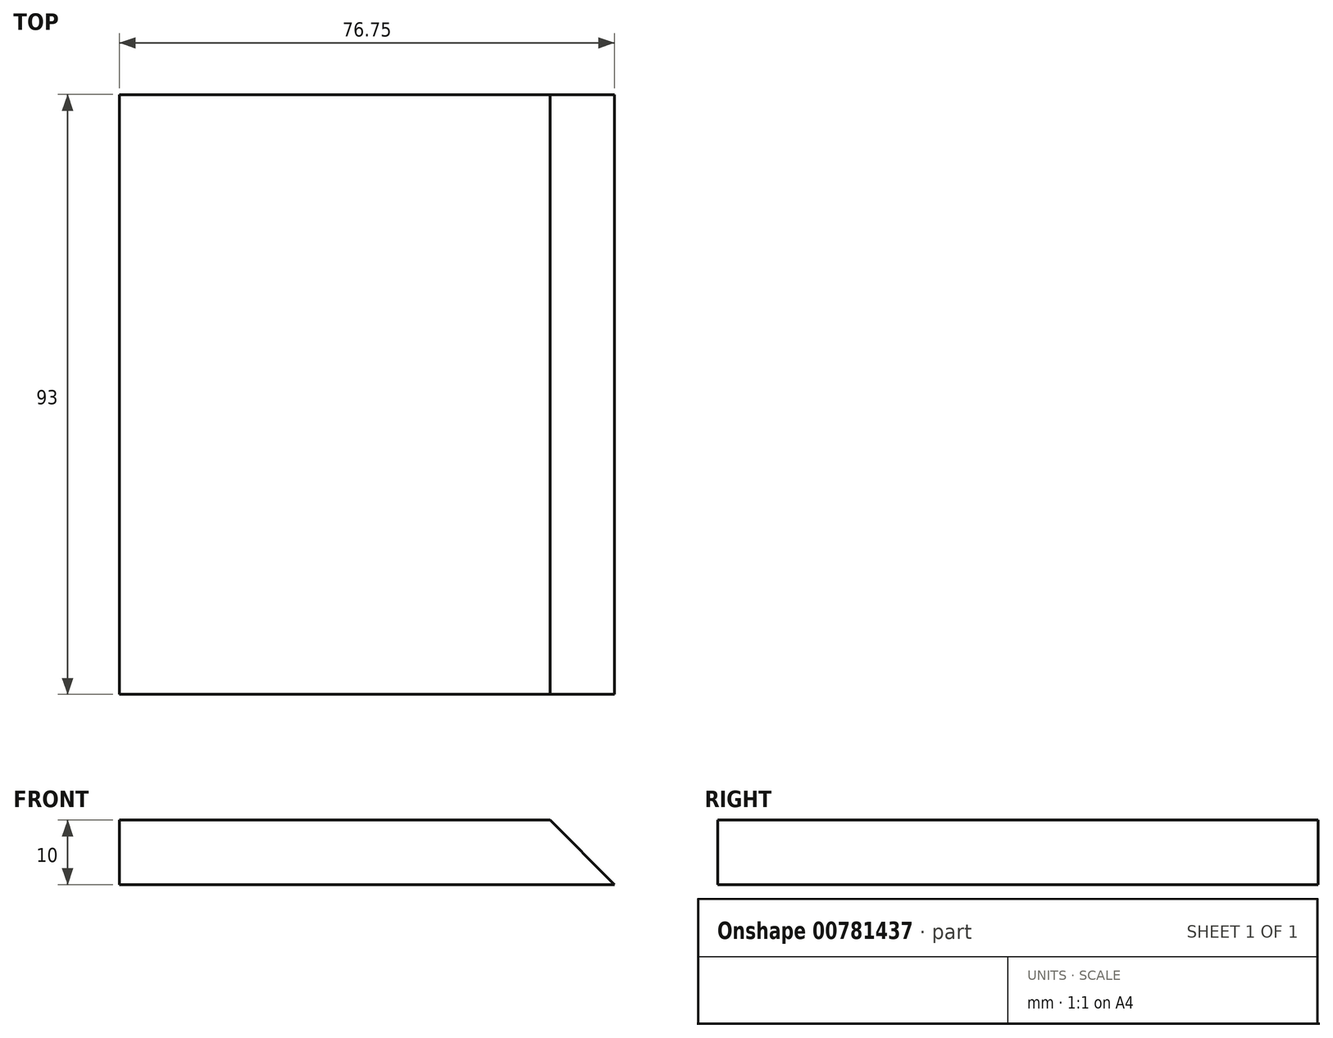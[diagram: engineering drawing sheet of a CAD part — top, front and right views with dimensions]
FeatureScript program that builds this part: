
annotation { "Feature Type Name" : "Feature", "Feature Type Description" : "" }
export const myFeature = defineFeature(function(context is Context, id is Id, definition is map)
    precondition{}
    {
        {
            var Q0;
            Q0=qCreatedBy(makeId("Top.planeOp"),FACE);
            var sketch = newSketch(context, id + "F0", { "sketchPlane" : qUnion([Q0])});
            skLineSegment(sketch, "E0.bottom", {"start": v(0, 0) * mm, "end": v(76.75, 0) * mm});
            skLineSegment(sketch, "E0.top", {"start": v(0, 93) * mm, "end": v(76.75, 93) * mm});
            skLineSegment(sketch, "E0.left", {"start": v(0, 0) * mm, "end": v(0, 93) * mm});
            skLineSegment(sketch, "E0.right", {"start": v(76.75, 0) * mm, "end": v(76.75, 93) * mm});
            skSolve(sketch);
        }
        {
            var Q0;
            Q0=makeQuery(id+"F0.imprint","IMPRINT",FACE,{"disambiguationData":[TD([[makeQuery(id+"F0.imprint","IMPRINT",EDGE,{"derivedFrom":sQuery(id+"F0.wireOp",EDGE,"E0.bottom")}),1.0]])]});
            extrude(context, id + "F1", {"entities" : qUnion([Q0]), "endBound" : BoundingType.SYMMETRIC, "depth" : 10 * mm, "offsetDistance" : 25.4 * mm});
        }
        {
            var Q0;
            Q0=makeQuery(id+"F1.opExtrude","SWEPT_FACE",FACE,{"disambiguationData":[OSD([sQuery(id+"F0.wireOp",EDGE,"E0.right")])]});
            var sketch = newSketch(context, id + "F2", { "sketchPlane" : qUnion([Q0])});
            skLineSegment(sketch, "E1.bottom", {"start": v(19.37, 5) * mm, "end": v(24, 5) * mm});
            skLineSegment(sketch, "E1.top", {"start": v(19.37, -5) * mm, "end": v(24, -5) * mm});
            skLineSegment(sketch, "E1.left", {"start": v(19.37, 5) * mm, "end": v(19.37, -5) * mm});
            skLineSegment(sketch, "E1.right", {"start": v(24, 5) * mm, "end": v(24, -5) * mm});
            skSolve(sketch);
        }
        {
            var Q0;
            Q0=makeQuery(id+"F1.opExtrude","CAP_EDGE",EDGE,{"disambiguationData":[OSD([sQuery(id+"F0.wireOp",EDGE,"E0.right")])],"isStart":false});
            chamfer(context, id + "F3", {"entities" : qUnion([Q0]), "width" : 10 * mm, "tangentPropagation" : true});
        }
    });
